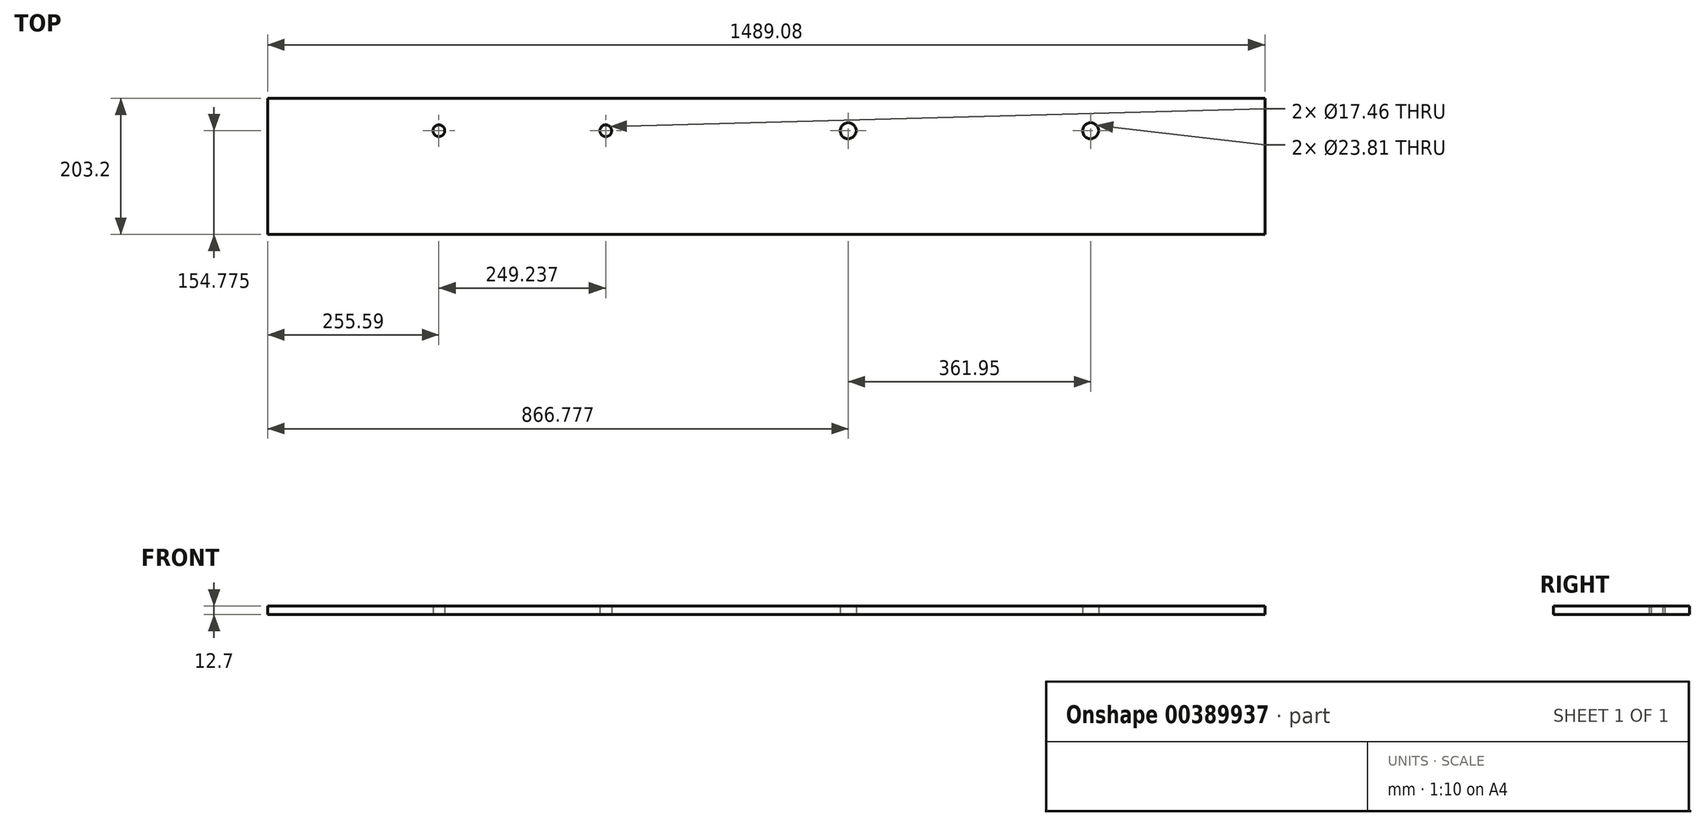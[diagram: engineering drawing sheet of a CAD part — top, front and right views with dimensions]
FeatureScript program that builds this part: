
annotation { "Feature Type Name" : "Feature", "Feature Type Description" : "" }
export const myFeature = defineFeature(function(context is Context, id is Id, definition is map)
    precondition{}
    {
        {
            var Q0;
            Q0=qCreatedBy(makeId("Top.planeOp"),FACE);
            var sketch = newSketch(context, id + "F0", { "sketchPlane" : qUnion([Q0])});
            skLineSegment(sketch, "E0.bottom", {"start": v(744.54, -101.6) * mm, "end": v(-744.54, -101.6) * mm});
            skLineSegment(sketch, "E0.top", {"start": v(744.54, 101.6) * mm, "end": v(-744.54, 101.6) * mm});
            skLineSegment(sketch, "E0.left", {"start": v(744.54, -101.6) * mm, "end": v(744.54, 101.6) * mm});
            skLineSegment(sketch, "E0.right", {"start": v(-744.54, -101.6) * mm, "end": v(-744.54, 101.6) * mm});
            skPoint(sketch, "E0.middle", {"position": v(0, 0) * mm});
            skCircle(sketch, "E1", {"center": v(-488.95, 53.17) * mm, "radius": 8.73 * mm});
            skCircle(sketch, "E2", {"center": v(-239.71, 53.17) * mm, "radius": 8.73 * mm});
            skCircle(sketch, "E3", {"center": v(122.24, 53.17) * mm, "radius": 11.9 * mm});
            skCircle(sketch, "E4", {"center": v(484.19, 53.17) * mm, "radius": 11.9 * mm});
            skSolve(sketch);
        }
        {
            var Q0;
            Q0=makeQuery(id+"F0.imprint","IMPRINT",FACE,{"disambiguationData":[TD([[makeQuery(id+"F0.imprint","IMPRINT",EDGE,{"derivedFrom":sQuery(id+"F0.wireOp",EDGE,"E0.bottom")}),-1.0]])]});
            extrude(context, id + "F1", {"entities" : qUnion([Q0]), "depth" : 12.7 * mm});
        }
    });
